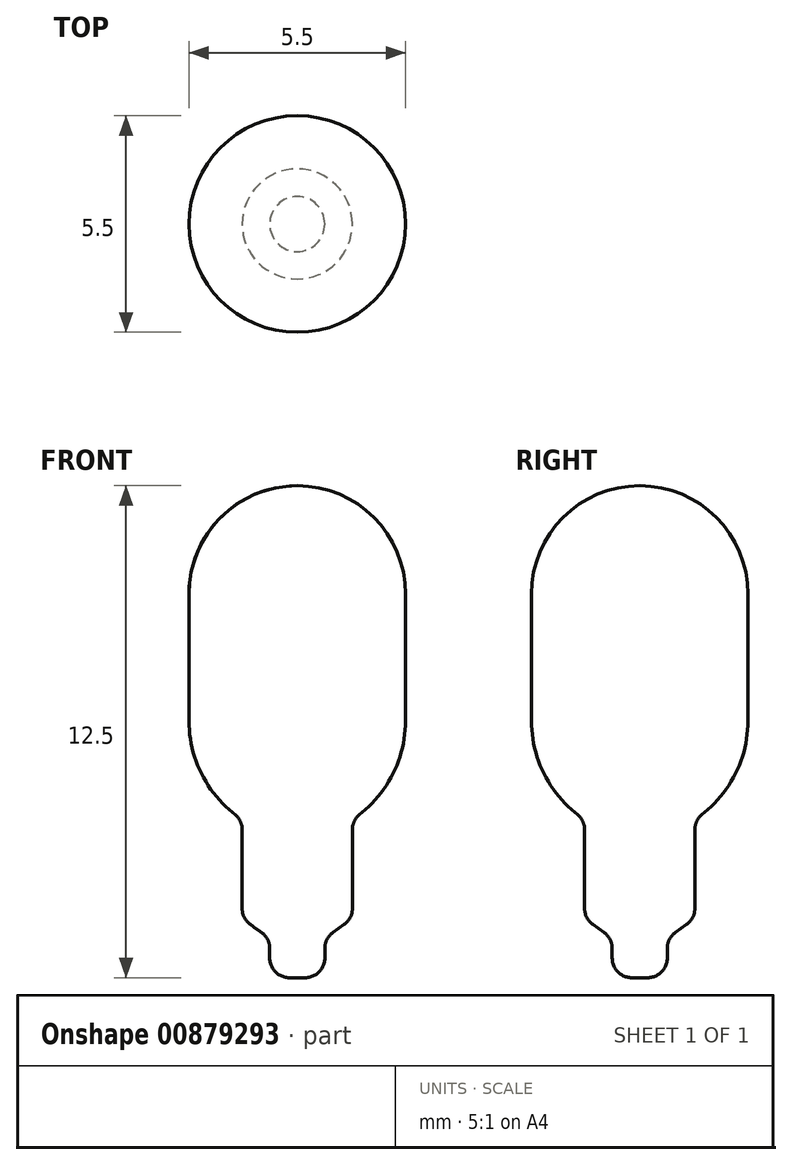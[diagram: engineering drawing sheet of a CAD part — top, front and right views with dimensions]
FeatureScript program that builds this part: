
annotation { "Feature Type Name" : "Feature", "Feature Type Description" : "" }
export const myFeature = defineFeature(function(context is Context, id is Id, definition is map)
    precondition{}
    {
        {
            var Q0;
            Q0=qCreatedBy(makeId("Front.planeOp"),FACE);
            var sketch = newSketch(context, id + "F0", { "sketchPlane" : qUnion([Q0])});
            skArc(sketch, "E0", {"start": v(0, -2.75) * mm, "mid": v(1.94, 1.94) * mm, "end": v(-2.75, 0) * mm});
            skLineSegment(sketch, "E1", {"start": v(-2.75, 0) * mm, "end": v(-2.75, -3.22) * mm});
            skLineSegment(sketch, "E2", {"start": v(-1.65, -5.55) * mm, "end": v(-1.58, -5.6) * mm});
            skLineSegment(sketch, "E3", {"start": v(-1.4, -5.99) * mm, "end": v(-1.4, -8) * mm});
            skLineSegment(sketch, "E4", {"start": v(-1.2, -8.4) * mm, "end": v(-0.9, -8.6) * mm});
            skLineSegment(sketch, "E5", {"start": v(-0.7, -9) * mm, "end": v(-0.7, -9.25) * mm});
            skLineSegment(sketch, "E6", {"start": v(-0.2, -9.75) * mm, "end": v(0, -9.75) * mm});
            skLineSegment(sketch, "E7", {"start": v(0, -9.75) * mm, "end": v(0, 2.75) * mm});
            skPoint(sketch, "E8.visualSharp", {"position": v(-2.75, -4.65) * mm});
            skArc(sketch, "E8.filletArc", {"start": v(-2.75, -3.22) * mm, "mid": v(-2.46, -4.51) * mm, "end": v(-1.65, -5.55) * mm});
            skPoint(sketch, "E9.visualSharp", {"position": v(-1.4, -5.75) * mm});
            skArc(sketch, "E9.filletArc", {"start": v(-1.4, -5.99) * mm, "mid": v(-1.45, -5.77) * mm, "end": v(-1.58, -5.6) * mm});
            skPoint(sketch, "E10.visualSharp", {"position": v(-1.4, -8.25) * mm});
            skArc(sketch, "E10.filletArc", {"start": v(-1.4, -8) * mm, "mid": v(-1.34, -8.22) * mm, "end": v(-1.2, -8.4) * mm});
            skPoint(sketch, "E11.visualSharp", {"position": v(-0.7, -8.75) * mm});
            skArc(sketch, "E11.filletArc", {"start": v(-0.7, -9) * mm, "mid": v(-0.76, -8.78) * mm, "end": v(-0.9, -8.6) * mm});
            skPoint(sketch, "E12.visualSharp", {"position": v(-0.7, -9.75) * mm});
            skArc(sketch, "E12.filletArc", {"start": v(-0.7, -9.25) * mm, "mid": v(-0.55, -9.6) * mm, "end": v(-0.2, -9.75) * mm});
            skSolve(sketch);
        }
        {
            var Q0;
            {var subQ5=sQuery(id+"F0.wireOp",EDGE,"E1");Q0=makeQuery(id+"F0.imprint","IMPRINT",FACE,{"disambiguationData":[TD([[makeQuery(id+"F0.imprint","IMPRINT",EDGE,{"derivedFrom":subQ5}),1.0]])]});}
            var Q1;
            Q1=sQuery(id+"F0.wireOp",EDGE,"E7");
            revolve(context, id + "F1", {"surfaceOperationType" : NewSurfaceOperationType.NEW, "entities" : qUnion([Q0]), "axis" : qUnion([Q1]), "revolveType" : RevolveType.FULL});
        }
    });
